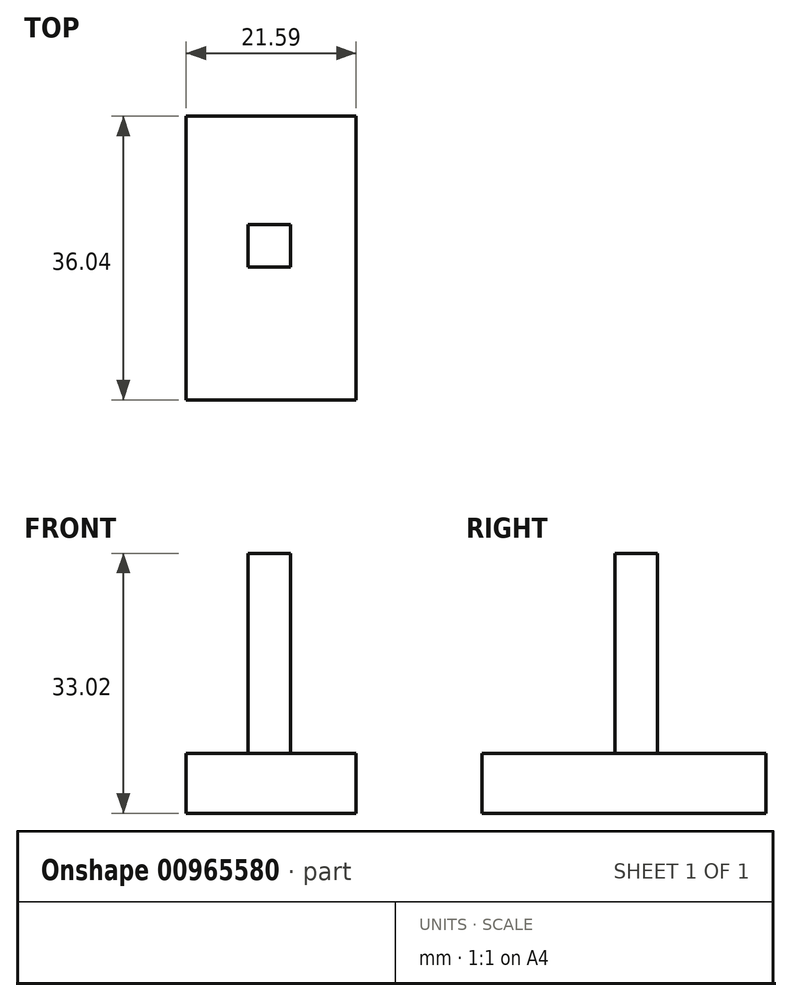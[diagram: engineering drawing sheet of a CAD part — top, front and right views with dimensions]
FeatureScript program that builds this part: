
annotation { "Feature Type Name" : "Feature", "Feature Type Description" : "" }
export const myFeature = defineFeature(function(context is Context, id is Id, definition is map)
    precondition{}
    {
        {
            var Q0;
            Q0=qCreatedBy(makeId("Top.planeOp"),FACE);
            var sketch = newSketch(context, id + "F0", { "sketchPlane" : qUnion([Q0])});
            skLineSegment(sketch, "E0.bottom", {"start": v(-26.9, 28.03) * mm, "end": v(-5.31, 28.03) * mm});
            skLineSegment(sketch, "E0.top", {"start": v(-26.9, -8) * mm, "end": v(-5.31, -8) * mm});
            skLineSegment(sketch, "E0.left", {"start": v(-26.9, 28.03) * mm, "end": v(-26.9, -8) * mm});
            skLineSegment(sketch, "E0.right", {"start": v(-5.31, 28.03) * mm, "end": v(-5.31, -8) * mm});
            skLineSegment(sketch, "E1.bottom", {"start": v(-19.07, 14.28) * mm, "end": v(-13.67, 14.28) * mm});
            skLineSegment(sketch, "E1.top", {"start": v(-19.07, 8.88) * mm, "end": v(-13.67, 8.88) * mm});
            skLineSegment(sketch, "E1.left", {"start": v(-19.07, 14.28) * mm, "end": v(-19.07, 8.88) * mm});
            skLineSegment(sketch, "E1.right", {"start": v(-13.67, 14.28) * mm, "end": v(-13.67, 8.88) * mm});
            skSolve(sketch);
        }
        {
            var Q0;
            Q0 = qSketchRegion(id + "F0", true);
            extrude(context, id + "F1", {"entities" : qUnion([Q0]), "depth" : 7.62 * mm, "offsetDistance" : 25.4 * mm});
        }
        {
            var Q0;
            Q0=makeQuery(id+"F0.imprint","IMPRINT",FACE,{"disambiguationData":[TD([[makeQuery(id+"F0.imprint","IMPRINT",EDGE,{"derivedFrom":sQuery(id+"F0.wireOp",EDGE,"E1.bottom")}),-1.0]])]});
            extrude(context, id + "F2", {"entities" : qUnion([Q0]), "operationType" : NewBodyOperationType.ADD, "depth" : 33.02 * mm, "offsetDistance" : 25.4 * mm});
        }
    });
